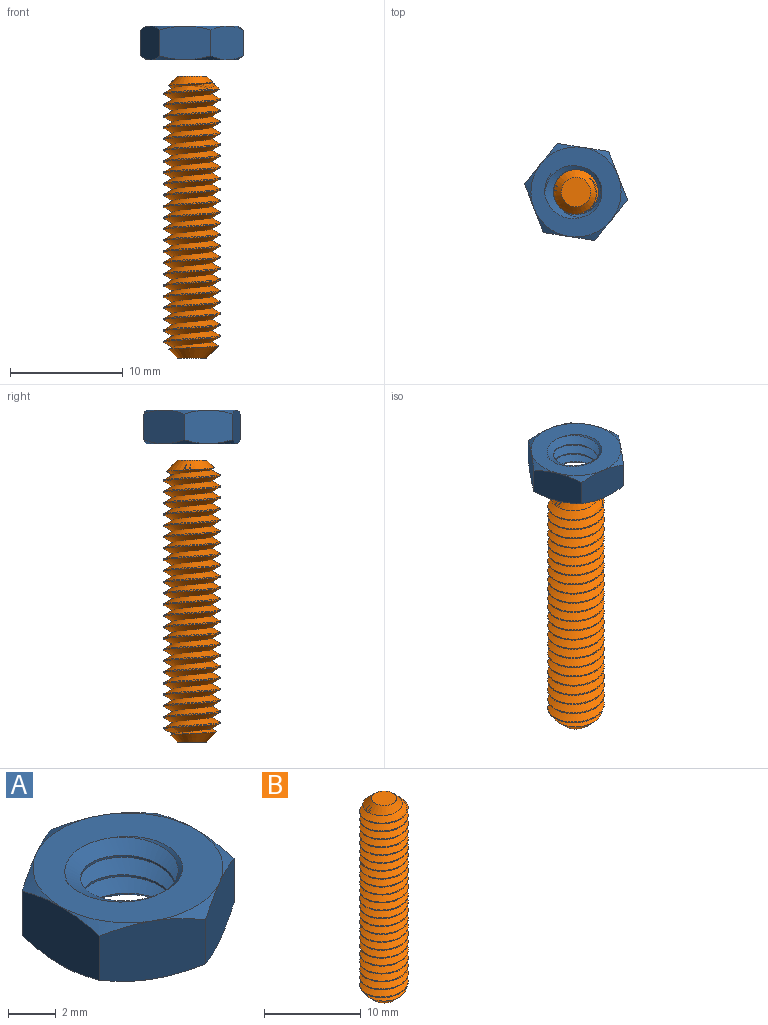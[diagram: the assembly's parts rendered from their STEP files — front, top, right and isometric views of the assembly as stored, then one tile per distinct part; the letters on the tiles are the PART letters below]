
ASSEMBLY  parts=2 mates=1
PART A: 25 faces, bbox 9.6x9.6x4.4 mm
  f0: plane 8.23x8.23mm, normal (0,0,1), area 31.6mm2, adj f5,f6,f8,f10,f12,f14,f22,f23
  f1: plane 8.23x8.23mm, normal (0,0,-1), area 31.6mm2, adj f3,f4,f7,f9,f11,f13,f21,f23
  f2: cylinder r=2mm len=4mm, axis (0,0,-1), area 3mm2, adj f21,f22,f23,f24
  f3: cone r=5.89mm half-angle=60deg, axis (0,0,1), area 1.6mm2, adj f1,f15,f20
  f4: cone r=5.89mm half-angle=60deg, axis (0,0,1), area 1.6mm2, adj f1,f15,f16
  f5: cone r=5.89mm half-angle=60deg, axis (0,0,-1), area 1.6mm2, adj f0,f15,f20
  f6: cone r=5.89mm half-angle=60deg, axis (0,0,-1), area 1.6mm2, adj f0,f15,f16
  f7: cone r=5.89mm half-angle=60deg, axis (0,0,1), area 1.6mm2, adj f1,f16,f17
  f8: cone r=5.89mm half-angle=60deg, axis (0,0,-1), area 1.6mm2, adj f0,f16,f17
  f9: cone r=5.89mm half-angle=60deg, axis (0,0,1), area 1.6mm2, adj f1,f17,f18
  f10: cone r=5.89mm half-angle=60deg, axis (0,0,-1), area 1.6mm2, adj f0,f17,f18
  f11: cone r=5.89mm half-angle=60deg, axis (0,0,1), area 1.6mm2, adj f1,f18,f19
  f12: cone r=5.89mm half-angle=60deg, axis (0,0,-1), area 1.6mm2, adj f0,f18,f19
  f13: cone r=5.89mm half-angle=60deg, axis (0,0,1), area 1.6mm2, adj f1,f19,f20
  f14: cone r=5.89mm half-angle=60deg, axis (0,0,-1), area 1.6mm2, adj f0,f19,f20
  f15: plane 5x3.38mm, normal (1,0,0), area 12.7mm2, adj f3,f4,f5,f6,f16,f20
  f16: plane 4.38x3.39mm, normal (0.5,-0.87,0), area 12.7mm2, adj f4,f6,f7,f8,f15,f17
  f17: plane 4.38x3.39mm, normal (-0.5,-0.87,0), area 12.7mm2, adj f7,f8,f9,f10,f16,f18
  f18: plane 5x3.38mm, normal (-1,0,0), area 12.7mm2, adj f9,f10,f11,f12,f17,f19
  f19: plane 4.38x3.39mm, normal (-0.5,0.87,0), area 12.7mm2, adj f11,f12,f13,f14,f18,f20
  f20: plane 4.38x3.39mm, normal (0.5,0.87,0), area 12.7mm2, adj f3,f5,f13,f14,f15,f19
  f21: cone r=2.3mm half-angle=45deg, axis (0,0,-1), area 1.6mm2, adj f1,f2,f23,f24
  f22: cone r=2mm half-angle=45deg, axis (0,0,1), area 1.6mm2, adj f0,f2,f23,f24
  f23: bspline ~6.42x5.56mm, area 39.3mm2, adj f0,f1,f2,f21,f22,f24
  f24: bspline ~6.42x5.56mm, area 39.2mm2, adj f0,f1,f2,f21,f22,f23
PART B: 9 faces, bbox 5x5.8x25.1 mm
  f0: cylinder r=2.5mm len=22.6mm, axis (0,0,-1), area -64.5mm2, adj f3,f4,f7,f8
  f1: plane 2.6x2.6mm, normal (0,0,1), area 5.3mm2, adj f3
  f2: plane 2.6x2.6mm, normal (0,0,-1), area 5.3mm2, adj f5
  f3: cone r=1.3mm half-angle=45deg, axis (0,0,-1), area 13.3mm2, adj f0,f1,f7,f8
  f4: cone r=2.5mm half-angle=45deg, axis (0,0,1), area 1.9mm2, adj f0,f5,f7,f8
  f5: cone r=2.5mm half-angle=45deg, axis (0,0,1), area 11.4mm2, adj f2,f4,f6,f8
  f6: plane 0.07x0.05mm, normal (0,1,0), area 0mm2, adj f5,f7,f8
  f7: bspline ~24.62x5.77mm, area 278mm2, adj f0,f3,f4,f6,f8
  f8: bspline ~24.62x5.77mm, area 277.4mm2, adj f0,f3,f4,f5,f6,f7
PLACE A rot(axis=(0,0,1),21.2deg) t=(0,0,26.47)mm
PLACE B at identity fixed
MATE cylindrical A.f2 <-> B.f0  axis (0,0,1) through (0,0,26.47)mm
